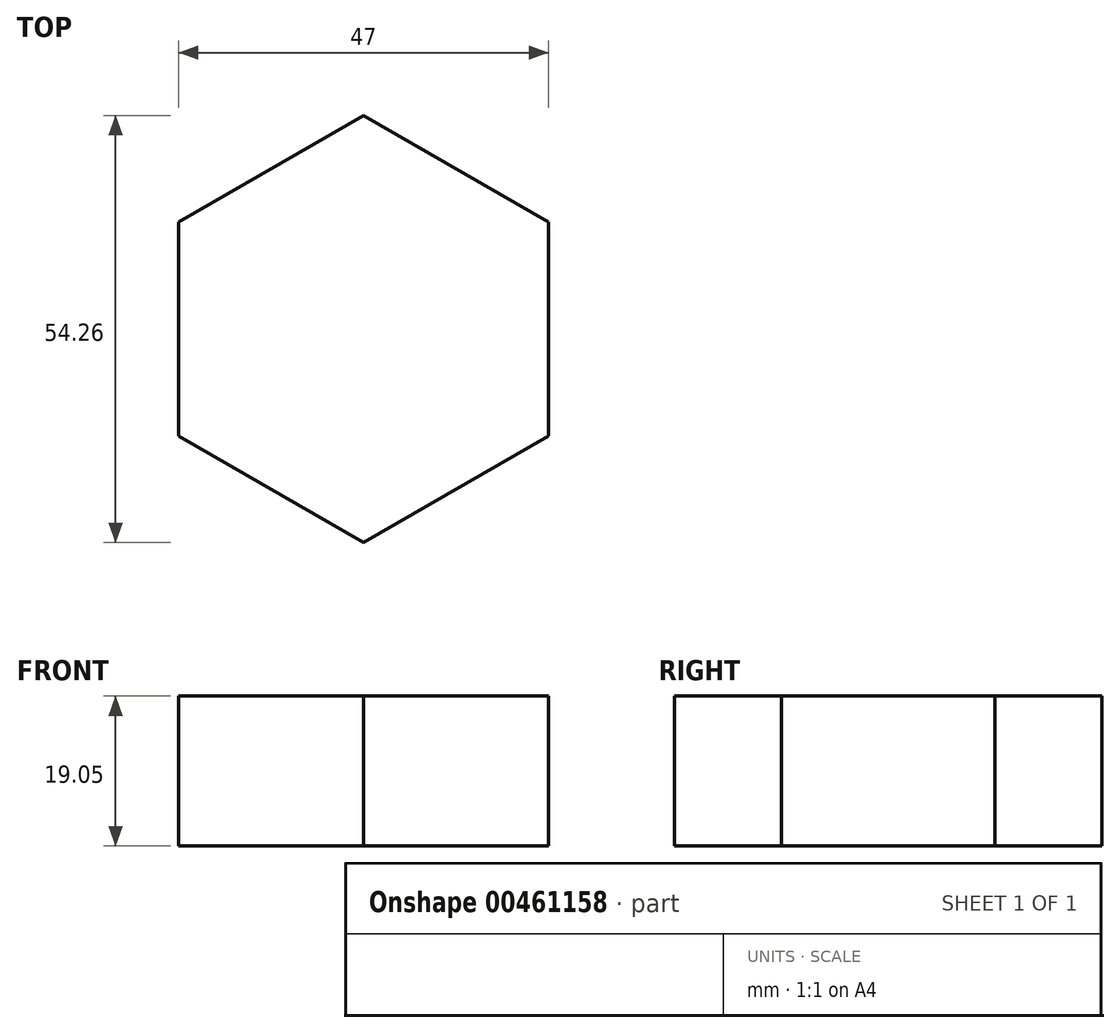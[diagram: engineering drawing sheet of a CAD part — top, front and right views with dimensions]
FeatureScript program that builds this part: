
annotation { "Feature Type Name" : "Feature", "Feature Type Description" : "" }
export const myFeature = defineFeature(function(context is Context, id is Id, definition is map)
    precondition{}
    {
        {
            var Q0;
            Q0=qCreatedBy(makeId("Top.planeOp"),FACE);
            var sketch = newSketch(context, id + "F0", { "sketchPlane" : qUnion([Q0])});
            skCircle(sketch, "E0.cCircle", {"center": v(0, 0) * mm, "radius": 23.5 * mm, "construction": true});
            skLineSegment(sketch, "E0.0", {"start": v(23.5, 13.56) * mm, "end": v(23.5, -13.56) * mm});
            skLineSegment(sketch, "E0.1", {"start": v(23.5, -13.56) * mm, "end": v(0, -27.13) * mm});
            skLineSegment(sketch, "E0.2", {"start": v(0, -27.13) * mm, "end": v(-23.5, -13.56) * mm});
            skLineSegment(sketch, "E0.3", {"start": v(-23.5, -13.56) * mm, "end": v(-23.5, 13.56) * mm});
            skLineSegment(sketch, "E0.4", {"start": v(-23.5, 13.56) * mm, "end": v(0, 27.13) * mm});
            skLineSegment(sketch, "E0.5", {"start": v(0, 27.13) * mm, "end": v(23.5, 13.56) * mm});
            skPoint(sketch, "E0.0.midPoint", {"position": v(23.5, 0) * mm});
            skSolve(sketch);
        }
        {
            var Q0;
            Q0=qSketchRegion(id+"F0",true);
            extrude(context, id + "F1", {"entities" : qUnion([Q0]), "depth" : 19.05 * mm});
        }
    });
